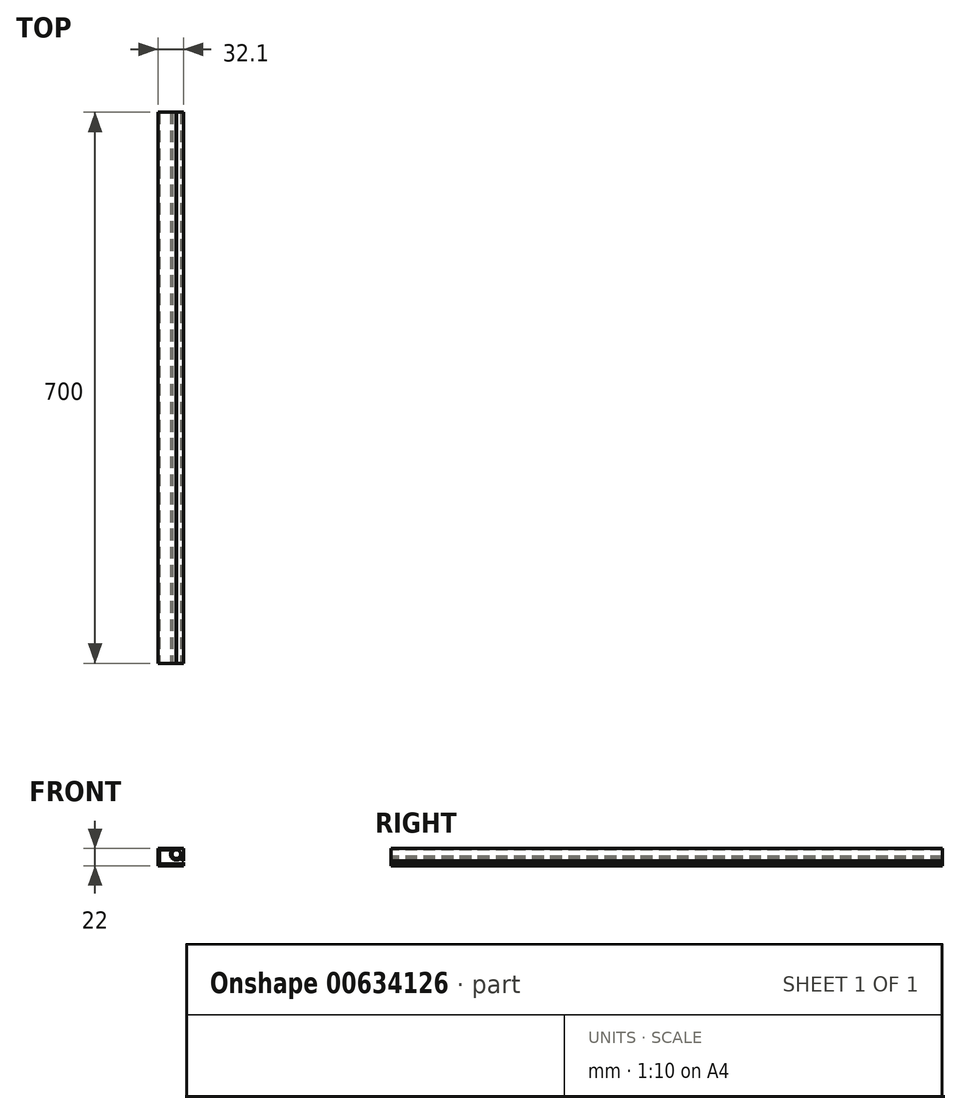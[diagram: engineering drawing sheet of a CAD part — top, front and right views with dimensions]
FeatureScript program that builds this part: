
annotation { "Feature Type Name" : "Feature", "Feature Type Description" : "" }
export const myFeature = defineFeature(function(context is Context, id is Id, definition is map)
    precondition{}
    {
        {
            var Q0;
            Q0=qCreatedBy(makeId("Front.planeOp"),FACE);
            var sketch = newSketch(context, id + "F0", { "sketchPlane" : qUnion([Q0])});
            skLineSegment(sketch, "E0.bottom", {"start": v(-15, 40) * mm, "end": v(15, 40) * mm});
            skLineSegment(sketch, "E0.top", {"start": v(-12, 0) * mm, "end": v(12, 0) * mm});
            skLineSegment(sketch, "E0.left", {"start": v(-15, 40) * mm, "end": v(-15, 37) * mm});
            skLineSegment(sketch, "E0.right", {"start": v(15, 37) * mm, "end": v(15, 3) * mm});
            skLineSegment(sketch, "E1.0", {"start": v(-15, 37) * mm, "end": v(3, 37) * mm});
            skLineSegment(sketch, "E1.1", {"start": v(-12, 6) * mm, "end": v(-12, 6) * mm});
            skLineSegment(sketch, "E1.2", {"start": v(-9, 3) * mm, "end": v(9, 3) * mm});
            skLineSegment(sketch, "E1.3", {"start": v(12, 29.6) * mm, "end": v(12, 6) * mm});
            skLineSegment(sketch, "E2.0", {"start": v(-15, 6) * mm, "end": v(-12, 6) * mm});
            skLineSegment(sketch, "E3", {"start": v(12, 40) * mm, "end": v(7.5, 40) * mm, "construction": true});
            skLineSegment(sketch, "E4", {"start": v(7, 34.8) * mm, "end": v(7, 40) * mm, "construction": true});
            skArc(sketch, "E5", {"start": v(7, 40) * mm, "mid": v(6.75, 29.6) * mm, "end": v(7.5, 39.98) * mm});
            skLineSegment(sketch, "E6.trimOffspring", {"start": v(-15, 6) * mm, "end": v(-15, 3) * mm});
            skPoint(sketch, "E7.orphan", {"position": v(5, 29.7) * mm});
            skPoint(sketch, "E8.visualSharp", {"position": v(15, 40) * mm});
            skArc(sketch, "E8.filletArc", {"start": v(15, 37) * mm, "mid": v(14.12, 39.12) * mm, "end": v(12, 40) * mm});
            skPoint(sketch, "E9.visualSharp", {"position": v(15, 0) * mm});
            skArc(sketch, "E9.filletArc", {"start": v(12, 0) * mm, "mid": v(14.12, 0.88) * mm, "end": v(15, 3) * mm});
            skArc(sketch, "E10.filletArc", {"start": v(9, 3) * mm, "mid": v(11.12, 3.88) * mm, "end": v(12, 6) * mm});
            skPoint(sketch, "E11.visualSharp", {"position": v(-12, 3) * mm});
            skArc(sketch, "E11.filletArc", {"start": v(-12, 6) * mm, "mid": v(-11.12, 3.88) * mm, "end": v(-9, 3) * mm});
            skPoint(sketch, "E12.visualSharp", {"position": v(-15, 0) * mm});
            skArc(sketch, "E12.filletArc", {"start": v(-15, 3) * mm, "mid": v(-14.12, 0.88) * mm, "end": v(-12, 0) * mm});
            skLineSegment(sketch, "E13.0", {"start": v(6.5, 34.8) * mm, "end": v(6.5, 39.8) * mm});
            skLineSegment(sketch, "E14.0", {"start": v(7.5, 34.8) * mm, "end": v(7.5, 40) * mm});
            skLineSegment(sketch, "E15", {"start": v(-15, 6) * mm, "end": v(-15, 16) * mm});
            skLineSegment(sketch, "E16", {"start": v(-15, 16) * mm, "end": v(-12, 16) * mm});
            skLineSegment(sketch, "E17", {"start": v(-12, 16) * mm, "end": v(-12, 6) * mm});
            skLineSegment(sketch, "E18", {"start": v(6.75, 29.6) * mm, "end": v(12, 29.6) * mm});
            skSolve(sketch);
        }
        {
            var Q0;
            Q0=qCreatedBy(makeId("Front.planeOp"),FACE);
            var sketch = newSketch(context, id + "F1", { "sketchPlane" : qUnion([Q0])});
            skLineSegment(sketch, "E19.1.1", {"start": v(7.5, 40) * mm, "end": v(-15, 40) * mm});
            skLineSegment(sketch, "E19.1.2", {"start": v(-15, 40) * mm, "end": v(-15, 37) * mm});
            skArc(sketch, "E19.2.8", {"start": v(-15, 3) * mm, "mid": v(-14.12, 0.88) * mm, "end": v(-12, 0) * mm, "construction": true});
            skLineSegment(sketch, "E19.2.9", {"start": v(-12, 0) * mm, "end": v(-5, 0) * mm});
            skLineSegment(sketch, "E19.2.13", {"start": v(17, 40) * mm, "end": v(8.5, 40) * mm});
            skLineSegment(sketch, "E19.3.0", {"start": v(-15, 18) * mm, "end": v(-15, 7.7) * mm});
            skPoint(sketch, "E20.2", {"position": v(6.5, 37.3) * mm});
            skPoint(sketch, "E21.orphan", {"position": v(6.5, 39.8) * mm});
            skPoint(sketch, "E19.0.2.end.orphan", {"position": v(7, 40) * mm});
            skPoint(sketch, "E22.orphan", {"position": v(12, 29.6) * mm});
            skPoint(sketch, "E23.orphan", {"position": v(7.5, 34.8) * mm});
            skPoint(sketch, "E20.0.start.orphan", {"position": v(6.5, 34.8) * mm});
            skLineSegment(sketch, "E24", {"start": v(-15, 37) * mm, "end": v(-15, 31) * mm});
            skLineSegment(sketch, "E25", {"start": v(0, 0) * mm, "end": v(0, 15) * mm, "construction": true});
            skLineSegment(sketch, "E26", {"start": v(7.5, 40) * mm, "end": v(7.5, 37.97) * mm});
            skLineSegment(sketch, "E27", {"start": v(8.5, 40) * mm, "end": v(8.5, 37.97) * mm});
            skLineSegment(sketch, "E28", {"start": v(15, 32.5) * mm, "end": v(8, 32.5) * mm, "construction": true});
            skPoint(sketch, "E29.orphan", {"position": v(7.6, 39) * mm});
            skLineSegment(sketch, "E30", {"start": v(8, 39) * mm, "end": v(8, 32.5) * mm, "construction": true});
            skPoint(sketch, "E19.3.3.end.orphan", {"position": v(-15, 16) * mm});
            skPoint(sketch, "E19.3.3.start.orphan", {"position": v(-12, 16) * mm});
            skLineSegment(sketch, "E31", {"start": v(-15, 3) * mm, "end": v(-15, 0) * mm});
            skLineSegment(sketch, "E32", {"start": v(-12, 0) * mm, "end": v(-15, 0) * mm});
            skLineSegment(sketch, "E33", {"start": v(-15, 40) * mm, "end": v(-15, 31) * mm, "construction": true});
            skLineSegment(sketch, "E34", {"start": v(-15, 40) * mm, "end": v(-15, 31) * mm});
            skLineSegment(sketch, "E35.trimOffspring", {"start": v(-15, 31) * mm, "end": v(-15, 26) * mm});
            skLineSegment(sketch, "E36.trimOffspring", {"start": v(-15, 29) * mm, "end": v(-15, 24) * mm});
            skPoint(sketch, "E37.orphan", {"position": v(12, 40) * mm});
            skPoint(sketch, "E38.orphan", {"position": v(12, 0) * mm});
            skLineSegment(sketch, "E39.0", {"start": v(13.1, 38) * mm, "end": v(13.1, 38) * mm});
            skLineSegment(sketch, "E40.1", {"start": v(-13, 2) * mm, "end": v(-11, 2) * mm, "construction": true});
            skLineSegment(sketch, "E41.0", {"start": v(-13, 38) * mm, "end": v(-13, 34) * mm});
            skArc(sketch, "E42", {"start": v(13.32, 33.87) * mm, "mid": v(11.56, 36.69) * mm, "end": v(8.5, 37.97) * mm});
            skLineSegment(sketch, "E43.0", {"start": v(29.42, 20) * mm, "end": v(-7, 20) * mm, "construction": true});
            skLineSegment(sketch, "E44.trimOffspring", {"start": v(-13, 0.17) * mm, "end": v(-13, 0) * mm});
            skArc(sketch, "E45.0", {"start": v(2.9, 38) * mm, "mid": v(3.81, 26.3) * mm, "end": v(15, 29.84) * mm});
            skLineSegment(sketch, "E46.trimOffspring", {"start": v(2.9, 38) * mm, "end": v(-13, 38) * mm});
            skLineSegment(sketch, "E47.trimOffspring", {"start": v(13.32, 33.87) * mm, "end": v(13.43, 31.7) * mm});
            skArc(sketch, "E48.trimOffspring", {"start": v(13.1, 38) * mm, "mid": v(13.1, 38) * mm, "end": v(13.1, 38) * mm});
            skArc(sketch, "E49.trimOffspring", {"start": v(7.5, 37.97) * mm, "mid": v(4.01, 28.73) * mm, "end": v(13.43, 31.7) * mm});
            skPoint(sketch, "E50.orphan", {"position": v(7.5, 39) * mm});
            skPoint(sketch, "E51.start.orphan", {"position": v(8.5, 39) * mm});
            skLineSegment(sketch, "E52.0", {"start": v(8, 0) * mm, "end": v(8, 13.5) * mm});
            skLineSegment(sketch, "E53.0", {"start": v(-5, 0) * mm, "end": v(-5, 13.5) * mm});
            skLineSegment(sketch, "E54.0", {"start": v(16.47, 12) * mm, "end": v(14.46, 12) * mm, "construction": true});
            skLineSegment(sketch, "E55.trimOffspring", {"start": v(12.84, 12) * mm, "end": v(10, 12) * mm});
            skLineSegment(sketch, "E56.0", {"start": v(1.5, 0) * mm, "end": v(1.5, 20) * mm, "construction": true});
            skLineSegment(sketch, "E57", {"start": v(1.5, 20) * mm, "end": v(-9.16, 15.5) * mm});
            skLineSegment(sketch, "E58", {"start": v(1.5, 20) * mm, "end": v(10.84, 15.5) * mm});
            skLineSegment(sketch, "E59.0", {"start": v(-9.16, 13.5) * mm, "end": v(-5, 13.5) * mm});
            skLineSegment(sketch, "E60", {"start": v(-9.16, 15.5) * mm, "end": v(-9.16, 13.5) * mm});
            skLineSegment(sketch, "E61", {"start": v(10.84, 15.5) * mm, "end": v(10.84, 13.5) * mm});
            skLineSegment(sketch, "E62.trimOffspring", {"start": v(8, 13.5) * mm, "end": v(10.84, 13.5) * mm});
            skLineSegment(sketch, "E63.trimOffspring", {"start": v(10, 2) * mm, "end": v(15, 2) * mm});
            skLineSegment(sketch, "E64.trimOffspring", {"start": v(8, 0) * mm, "end": v(17, 0) * mm});
            skLineSegment(sketch, "E65.0", {"start": v(10, 2) * mm, "end": v(10, 12) * mm});
            skLineSegment(sketch, "E66.0", {"start": v(1.55, 22.2) * mm, "end": v(-7, 18.58) * mm});
            skLineSegment(sketch, "E66.1", {"start": v(1.55, 22.2) * mm, "end": v(12.84, 16.75) * mm});
            skLineSegment(sketch, "E67.0", {"start": v(-11.16, 16.82) * mm, "end": v(-11.16, 15.5) * mm});
            skLineSegment(sketch, "E68.0", {"start": v(-13, 11.5) * mm, "end": v(-7, 11.5) * mm});
            skLineSegment(sketch, "E69", {"start": v(-11.16, 15.5) * mm, "end": v(-11.16, 13.5) * mm});
            skLineSegment(sketch, "E70.0", {"start": v(12.84, 16.75) * mm, "end": v(12.84, 12) * mm});
            skLineSegment(sketch, "E71.0", {"start": v(-13, 6.7) * mm, "end": v(-7, 6.7) * mm, "construction": true});
            skLineSegment(sketch, "E72.0", {"start": v(-15, 7.7) * mm, "end": v(-13, 7.7) * mm});
            skLineSegment(sketch, "E73.0", {"start": v(-15, 5.7) * mm, "end": v(-11, 5.7) * mm});
            skLineSegment(sketch, "E74.0", {"start": v(-15, 3.7) * mm, "end": v(-13, 3.7) * mm, "construction": true});
            skLineSegment(sketch, "E75.trimOffspring", {"start": v(-15, 5.7) * mm, "end": v(-15, 3) * mm});
            skLineSegment(sketch, "E76.trimOffspring", {"start": v(-13, 3.7) * mm, "end": v(-13, 2) * mm, "construction": true});
            skLineSegment(sketch, "E77.trimOffspring", {"start": v(-11, 5.7) * mm, "end": v(-11, 2) * mm});
            skLineSegment(sketch, "E78.0", {"start": v(-13, 13.5) * mm, "end": v(-11.16, 13.5) * mm});
            skLineSegment(sketch, "E79.trimOffspring", {"start": v(-9.16, 13.5) * mm, "end": v(-7, 13.5) * mm});
            skLineSegment(sketch, "E80.trimOffspring", {"start": v(-13, 11.5) * mm, "end": v(-13, 7.7) * mm});
            skLineSegment(sketch, "E81.0", {"start": v(-7, 11.5) * mm, "end": v(-7, 3.7) * mm});
            skLineSegment(sketch, "E82.trimOffspring", {"start": v(-11, 3.7) * mm, "end": v(-7, 3.7) * mm});
            skLineSegment(sketch, "E83.0", {"start": v(17, 40) * mm, "end": v(17, 0) * mm});
            skPoint(sketch, "E84.orphan", {"position": v(17.1, 0) * mm});
            skLineSegment(sketch, "E85.trimOffspring", {"start": v(15, 29.84) * mm, "end": v(15, 2) * mm});
            skPoint(sketch, "E86.start.orphan", {"position": v(15, 40) * mm});
            skLineSegment(sketch, "E87", {"start": v(-13, 13.5) * mm, "end": v(-13, 18) * mm});
            skLineSegment(sketch, "E88.trimOffspring", {"start": v(-15, 22) * mm, "end": v(-15, 21.16) * mm, "construction": true});
            skLineSegment(sketch, "E89.trimOffspring", {"start": v(-15, 22) * mm, "end": v(-15, 18) * mm});
            skPoint(sketch, "E90.start.orphan", {"position": v(-12, 28) * mm});
            skPoint(sketch, "E91.orphan", {"position": v(-12, 29) * mm});
            skLineSegment(sketch, "E92.0", {"start": v(-9, 26) * mm, "end": v(-11, 26) * mm});
            skLineSegment(sketch, "E93.0", {"start": v(-11, 24) * mm, "end": v(-13, 24) * mm});
            skLineSegment(sketch, "E94", {"start": v(-9, 20) * mm, "end": v(-9, 26) * mm});
            skLineSegment(sketch, "E95.0", {"start": v(-11, 20) * mm, "end": v(-11, 22) * mm});
            skLineSegment(sketch, "E96.trimOffspring", {"start": v(-11, 24) * mm, "end": v(-11, 26) * mm});
            skLineSegment(sketch, "E97.trimOffspring", {"start": v(-13, 28) * mm, "end": v(-13, 34) * mm});
            skLineSegment(sketch, "E98", {"start": v(-15, 22) * mm, "end": v(-11, 22) * mm});
            skLineSegment(sketch, "E99", {"start": v(-13, 24) * mm, "end": v(-15, 24) * mm});
            skLineSegment(sketch, "E100.0", {"start": v(-7, 18.58) * mm, "end": v(-7, 28) * mm});
            skLineSegment(sketch, "E101.0", {"start": v(-13, 18) * mm, "end": v(-8.36, 18) * mm});
            skLineSegment(sketch, "E102.trimOffspring", {"start": v(-8.36, 18) * mm, "end": v(-11.16, 16.82) * mm});
            skLineSegment(sketch, "E103.0", {"start": v(-11, 20) * mm, "end": v(-9, 20) * mm});
            skLineSegment(sketch, "E104.0", {"start": v(-7, 28) * mm, "end": v(-13, 28) * mm});
            skSolve(sketch);
        }
        {
            var Q0;
            Q0=qSketchRegion(id+"F1",true);
            extrude(context, id + "F2", {"entities" : qUnion([Q0]), "oppositeDirection" : true, "depth" : 1910 * mm, "offsetDistance" : 25 * mm});
        }
        {
            var Q0;
            Q0=makeQuery(id+"F1.imprint","IMPRINT",FACE,{"disambiguationData":[TD([[makeQuery(id+"F1.imprint","IMPRINT",EDGE,{"derivedFrom":sQuery(id+"F1.wireOp",EDGE,"E19.1.1")}),1.0]])]});
            var sketch = newSketch(context, id + "F3", { "sketchPlane" : qUnion([Q0])});
            skLineSegment(sketch, "E105.0", {"start": v(-13.5, 18) * mm, "end": v(-13.5, -0.51) * mm});
            skSolve(sketch);
        }
        {
            var Q0;
            Q0=makeQuery(id+"F3.imprint","IMPRINT",FACE,{"disambiguationData":[TD([[makeQuery(id+"F3.imprint","IMPRINT",EDGE,{"derivedFrom":makeQuery(id+"F1.imprint","IMPRINT",EDGE,{"derivedFrom":sQuery(id+"F1.wireOp",EDGE,"E19.1.1")})}),1.0]])]});
            var sketch = newSketch(context, id + "F4", { "sketchPlane" : qUnion([Q0])});
            skLineSegment(sketch, "E106.0", {"start": v(-17, 40) * mm, "end": v(-25.5, 40) * mm});
            skLineSegment(sketch, "E107.0", {"start": v(-49.1, 40) * mm, "end": v(-49.1, 18) * mm});
            skLineSegment(sketch, "E108.0", {"start": v(-17, 40) * mm, "end": v(-17, 18) * mm});
            skPoint(sketch, "E109.orphan", {"position": v(7.5, 40) * mm});
            skLineSegment(sketch, "E110.1", {"start": v(-19, 29.83) * mm, "end": v(-19, 20) * mm});
            skLineSegment(sketch, "E110.3", {"start": v(-47.1, 38) * mm, "end": v(-47.1, 20) * mm});
            skArc(sketch, "E111.0", {"start": v(7.5, 37.97) * mm, "mid": v(4.01, 28.73) * mm, "end": v(13.43, 31.7) * mm, "construction": true});
            skLineSegment(sketch, "E112.0", {"start": v(17, 40) * mm, "end": v(8.5, 40) * mm});
            skLineSegment(sketch, "E113.0", {"start": v(7.5, 40) * mm, "end": v(-15, 40) * mm});
            skLineSegment(sketch, "E114.0", {"start": v(-26.6, 40) * mm, "end": v(-26.6, 37.97) * mm});
            skLineSegment(sketch, "E115.0", {"start": v(-25.5, 40) * mm, "end": v(-25.5, 37.98) * mm});
            skLineSegment(sketch, "E116.0", {"start": v(-7, 18.58) * mm, "end": v(-7, 28) * mm});
            skLineSegment(sketch, "E117", {"start": v(-47.1, 23.29) * mm, "end": v(15, 23.29) * mm, "construction": true});
            skPoint(sketch, "E118.orphan", {"position": v(-7, 23.29) * mm});
            skLineSegment(sketch, "E119", {"start": v(8, 32.5) * mm, "end": v(2.5, 32.5) * mm});
            skLineSegment(sketch, "E120.0", {"start": v(8, 39) * mm, "end": v(8, 32.5) * mm});
            skLineSegment(sketch, "E120.1", {"start": v(17, 40) * mm, "end": v(17, 0) * mm});
            skLineSegment(sketch, "E121.trimOffspring", {"start": v(-17, 32.5) * mm, "end": v(-26, 32.5) * mm, "construction": true});
            skArc(sketch, "E122", {"start": v(-26.6, 37.97) * mm, "mid": v(-25.95, 27.01) * mm, "end": v(-25.5, 37.98) * mm});
            skArc(sketch, "E123.0", {"start": v(-31.1, 38) * mm, "mid": v(-30.2, 26.3) * mm, "end": v(-19, 29.83) * mm});
            skLineSegment(sketch, "E124.trimOffspring", {"start": v(-26.6, 40) * mm, "end": v(-49.1, 40) * mm});
            skLineSegment(sketch, "E125.trimOffspring", {"start": v(-26.6, 27.05) * mm, "end": v(-26.6, 20) * mm, "construction": true});
            skLineSegment(sketch, "E126.trimOffspring", {"start": v(-25.5, 27.04) * mm, "end": v(-25.5, 20) * mm, "construction": true});
            skLineSegment(sketch, "E127.trimOffspring", {"start": v(-31.1, 38) * mm, "end": v(-47.1, 38) * mm});
            skLineSegment(sketch, "E128.0", {"start": v(-49.1, 18) * mm, "end": v(-17, 18) * mm});
            skPoint(sketch, "E129.orphan", {"position": v(-8.36, 18) * mm});
            skPoint(sketch, "E130.orphan", {"position": v(-13, 18) * mm});
            skLineSegment(sketch, "E131.0", {"start": v(-47.1, 20) * mm, "end": v(-19, 20) * mm});
            skSolve(sketch);
        }
        {
            var Q0;
            Q0=makeQuery(id+"F3.imprint","IMPRINT",FACE,{"disambiguationData":[TD([[makeQuery(id+"F3.imprint","IMPRINT",EDGE,{"derivedFrom":makeQuery(id+"F1.imprint","IMPRINT",EDGE,{"derivedFrom":sQuery(id+"F1.wireOp",EDGE,"E19.1.1")})}),1.0]])]});
            var sketch = newSketch(context, id + "F5", { "sketchPlane" : qUnion([Q0])});
            skLineSegment(sketch, "E132.0", {"start": v(-9, 20) * mm, "end": v(-9, 26) * mm});
            skLineSegment(sketch, "E132.2", {"start": v(-11, 24) * mm, "end": v(-11, 26) * mm});
            skLineSegment(sketch, "E132.3", {"start": v(-9, 26) * mm, "end": v(-11, 26) * mm});
            skLineSegment(sketch, "E132.4", {"start": v(-11, 24) * mm, "end": v(-13, 24) * mm});
            skLineSegment(sketch, "E132.6", {"start": v(-13, 24) * mm, "end": v(-19, 24) * mm});
            skLineSegment(sketch, "E132.7", {"start": v(-11, 20) * mm, "end": v(-11, 22) * mm});
            skLineSegment(sketch, "E132.8", {"start": v(-19, 22) * mm, "end": v(-11, 22) * mm});
            skLineSegment(sketch, "E133.0", {"start": v(-19, 22) * mm, "end": v(-19, 20) * mm});
            skPoint(sketch, "E134.orphan", {"position": v(-15, 24) * mm});
            skPoint(sketch, "E135.orphan", {"position": v(-19, 29.83) * mm});
            skLineSegment(sketch, "E136.0", {"start": v(-21, 26) * mm, "end": v(-21, 20) * mm});
            skLineSegment(sketch, "E137", {"start": v(-21, 26) * mm, "end": v(-19, 26) * mm});
            skLineSegment(sketch, "E138.0", {"start": v(-19, 26) * mm, "end": v(-19, 24) * mm});
            skPoint(sketch, "E139.orphan", {"position": v(-15, 22) * mm});
            skLineSegment(sketch, "E140", {"start": v(-21, 20) * mm, "end": v(-19, 20) * mm});
            skSolve(sketch);
        }
        {
            var Q0;
            Q0=makeQuery(id+"F4.imprint","IMPRINT",FACE,{"disambiguationData":[TD([[makeQuery(id+"F4.imprint","IMPRINT",EDGE,{"derivedFrom":sQuery(id+"F4.wireOp",EDGE,"E106.0")}),1.0]])]});
            var sketch = newSketch(context, id + "F6", { "sketchPlane" : qUnion([Q0])});
            skLineSegment(sketch, "E141.0.0", {"start": v(-26.6, 37.97) * mm, "end": v(-26.6, 40) * mm});
            skLineSegment(sketch, "E141.0.1", {"start": v(-26.6, 40) * mm, "end": v(-49.1, 40) * mm});
            skLineSegment(sketch, "E141.0.2", {"start": v(-49.1, 40) * mm, "end": v(-49.1, 18) * mm});
            skLineSegment(sketch, "E141.0.3", {"start": v(-49.1, 18) * mm, "end": v(-17, 18) * mm});
            skLineSegment(sketch, "E141.0.4", {"start": v(-17, 18) * mm, "end": v(-17, 22) * mm});
            skLineSegment(sketch, "E141.0.5", {"start": v(-17, 40) * mm, "end": v(-25.5, 40) * mm});
            skLineSegment(sketch, "E141.0.6", {"start": v(-25.5, 40) * mm, "end": v(-25.5, 37.98) * mm});
            skArc(sketch, "E141.0.7", {"start": v(-25.5, 37.98) * mm, "mid": v(-25.95, 27.01) * mm, "end": v(-26.6, 37.97) * mm});
            skPoint(sketch, "E142.0", {"position": v(-30.2, 26.3) * mm});
            skArc(sketch, "E143.0", {"start": v(-31.1, 38) * mm, "mid": v(-30.2, 26.3) * mm, "end": v(-19, 29.83) * mm});
            skLineSegment(sketch, "E144.0", {"start": v(-47.1, 20) * mm, "end": v(-19, 20) * mm});
            skLineSegment(sketch, "E145.0", {"start": v(-47.1, 38) * mm, "end": v(-47.1, 20) * mm});
            skLineSegment(sketch, "E146.0", {"start": v(-19, 22) * mm, "end": v(-17, 22) * mm});
            skLineSegment(sketch, "E147.0", {"start": v(-17, 24) * mm, "end": v(-19, 24) * mm});
            skLineSegment(sketch, "E148.0", {"start": v(-19, 29.83) * mm, "end": v(-19, 24) * mm});
            skLineSegment(sketch, "E149.0", {"start": v(-31.1, 38) * mm, "end": v(-47.1, 38) * mm});
            skPoint(sketch, "E150.orphan", {"position": v(-13, 24) * mm});
            skPoint(sketch, "E151.orphan", {"position": v(-11, 22) * mm});
            skLineSegment(sketch, "E152.trimOffspring", {"start": v(-19, 22) * mm, "end": v(-19, 20) * mm});
            skLineSegment(sketch, "E153.trimOffspring", {"start": v(-17, 24) * mm, "end": v(-17, 40) * mm});
            skSolve(sketch);
        }
        {
            var Q0;
            Q0 = qSketchRegion(id + "F6", true);
            extrude(context, id + "F7", {"entities" : qUnion([Q0]), "oppositeDirection" : true, "depth" : 700 * mm, "offsetDistance" : 25 * mm});
        }
        {
            var Q0;
            Q0=makeQuery(id+"F1.imprint","IMPRINT",FACE,{"disambiguationData":[TD([[makeQuery(id+"F1.imprint","IMPRINT",EDGE,{"derivedFrom":sQuery(id+"F1.wireOp",EDGE,"E19.1.1")}),1.0]])]});
            var sketch = newSketch(context, id + "F8", { "sketchPlane" : qUnion([Q0])});
            skLineSegment(sketch, "E154.0", {"start": v(17, 40) * mm, "end": v(17, 0) * mm});
            skLineSegment(sketch, "E155.0", {"start": v(17, 40) * mm, "end": v(-15, 40) * mm});
            skLineSegment(sketch, "E155.1", {"start": v(-15, 0) * mm, "end": v(17, 0) * mm});
            skLineSegment(sketch, "E155.2", {"start": v(-15, 40) * mm, "end": v(-15, 3) * mm});
            skPoint(sketch, "E156.orphan", {"position": v(7.5, 40) * mm});
            skPoint(sketch, "E157.orphan", {"position": v(-15, 18) * mm});
            skPoint(sketch, "E158.orphan", {"position": v(-12, 0) * mm});
            skLineSegment(sketch, "E159.0", {"start": v(-15, 3) * mm, "end": v(-15, 0) * mm});
            skPoint(sketch, "E160.orphan", {"position": v(-15, 7.7) * mm});
            skPoint(sketch, "E161.orphan", {"position": v(-5, 0) * mm});
            skSolve(sketch);
        }
        {
            var Q0;
            Q0 = qSketchRegion(id + "F8", true);
            extrude(context, id + "F9", {"entities" : qUnion([Q0]), "operationType" : NewBodyOperationType.REMOVE, "oppositeDirection" : true, "depth" : 2000 * mm, "offsetDistance" : 25 * mm});
        }
    });
